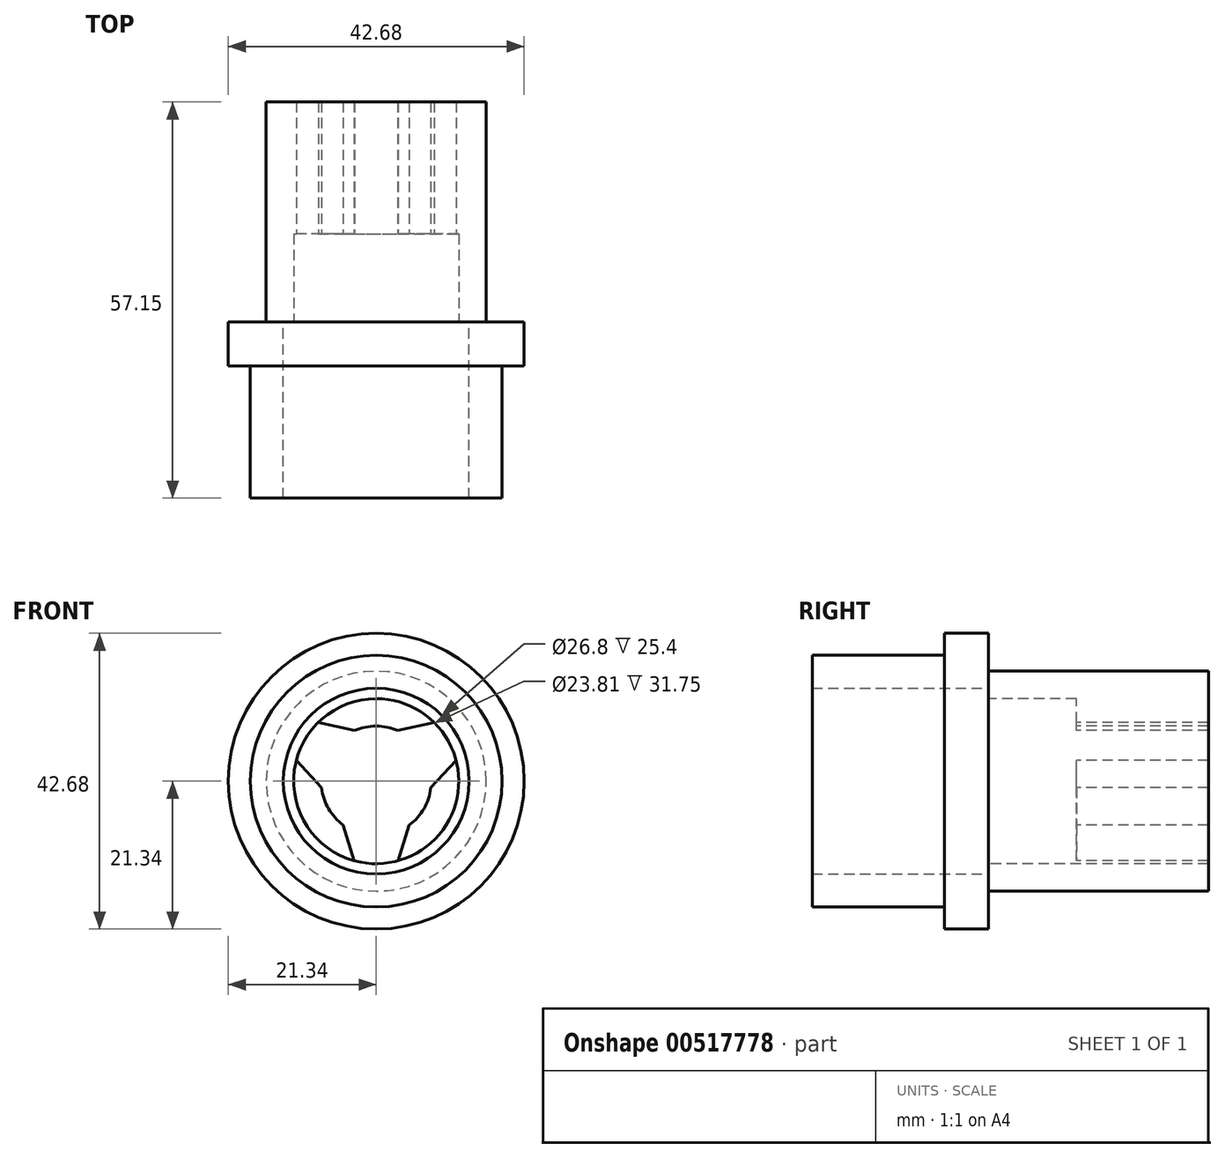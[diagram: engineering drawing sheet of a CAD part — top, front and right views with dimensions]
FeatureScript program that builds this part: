
annotation { "Feature Type Name" : "Feature", "Feature Type Description" : "" }
export const myFeature = defineFeature(function(context is Context, id is Id, definition is map)
    precondition{}
    {
        {
            var Q0;
            Q0=qCreatedBy(makeId("Front.planeOp"),FACE);
            var sketch = newSketch(context, id + "F0", { "sketchPlane" : qUnion([Q0])});
            skCircle(sketch, "E0", {"center": v(0, 0) * mm, "radius": 13.4 * mm});
            skCircle(sketch, "E1", {"center": v(0, 0) * mm, "radius": 18.16 * mm});
            skSolve(sketch);
        }
        {
            var Q0;
            Q0 = qSketchRegion(id + "F0", true);
            extrude(context, id + "F1", {"entities" : qUnion([Q0]), "depth" : 19.05 * mm, "offsetDistance" : 25.4 * mm});
        }
        {
            var Q0;
            Q0=qCreatedBy(makeId("Front.planeOp"),FACE);
            var sketch = newSketch(context, id + "F2", { "sketchPlane" : qUnion([Q0])});
            skCircle(sketch, "E2.0", {"center": v(0, 0) * mm, "radius": 13.4 * mm});
            skCircle(sketch, "E3", {"center": v(0, 0) * mm, "radius": 21.34 * mm});
            skSolve(sketch);
        }
        {
            var Q0;
            Q0 = qSketchRegion(id + "F2", true);
            extrude(context, id + "F3", {"entities" : qUnion([Q0]), "operationType" : NewBodyOperationType.ADD, "oppositeDirection" : true, "depth" : 6.35 * mm, "offsetDistance" : 25.4 * mm});
        }
        {
            var Q0;
            Q0=makeQuery(id+"F3.opExtrude","CAP_FACE",FACE,{"disambiguationData":[OSD([sQuery(id+"F2.wireOp",EDGE,"E2.0"),sQuery(id+"F2.wireOp",EDGE,"E3")])],"isStart":false});
            var sketch = newSketch(context, id + "F4", { "sketchPlane" : qUnion([Q0])});
            skCircle(sketch, "E4", {"center": v(0, 0) * mm, "radius": 11.9 * mm});
            skCircle(sketch, "E5", {"center": v(0, 0) * mm, "radius": 15.88 * mm});
            skSolve(sketch);
        }
        {
            var Q0;
            Q0 = qSketchRegion(id + "F4", true);
            extrude(context, id + "F5", {"entities" : qUnion([Q0]), "operationType" : NewBodyOperationType.ADD, "depth" : 12.7 * mm, "offsetDistance" : 25.4 * mm});
        }
        {
            var Q0;
            Q0=makeQuery(id+"F5.opExtrude","CAP_FACE",FACE,{"disambiguationData":[OSD([sQuery(id+"F4.wireOp",EDGE,"E4"),sQuery(id+"F4.wireOp",EDGE,"E5")])],"isStart":false});
            var sketch = newSketch(context, id + "F6", { "sketchPlane" : qUnion([Q0])});
            skCircle(sketch, "E6.0", {"center": v(0, 0) * mm, "radius": 15.88 * mm});
            skArc(sketch, "E7", {"start": v(-7.88, -0.95) * mm, "mid": v(-6.87, -3.97) * mm, "end": v(-4.76, -6.35) * mm});
            skLineSegment(sketch, "E8", {"start": v(0, 0) * mm, "end": v(0, -15.88) * mm, "construction": true});
            skLineSegment(sketch, "E9", {"start": v(0, 0) * mm, "end": v(-13.75, 7.94) * mm, "construction": true});
            skLineSegment(sketch, "E10", {"start": v(0, 0) * mm, "end": v(13.75, 7.94) * mm, "construction": true});
            skLineSegment(sketch, "E11", {"start": v(-3.12, 7.3) * mm, "end": v(-8.35, 8.49) * mm});
            skLineSegment(sketch, "E12", {"start": v(-7.88, -0.95) * mm, "end": v(-11.53, 2.99) * mm});
            skLineSegment(sketch, "E13", {"start": v(-4.76, -6.35) * mm, "end": v(-3.18, -11.48) * mm});
            skLineSegment(sketch, "E14", {"start": v(4.76, -6.35) * mm, "end": v(3.18, -11.48) * mm});
            skLineSegment(sketch, "E15", {"start": v(7.88, -0.95) * mm, "end": v(11.53, 2.99) * mm});
            skLineSegment(sketch, "E16", {"start": v(3.12, 7.3) * mm, "end": v(8.35, 8.49) * mm});
            skArc(sketch, "E17.0", {"start": v(-8.35, 8.49) * mm, "mid": v(-10.31, 5.95) * mm, "end": v(-11.53, 2.99) * mm});
            skArc(sketch, "E18.trimOffspring", {"start": v(3.12, 7.3) * mm, "mid": v(0, 7.94) * mm, "end": v(-3.12, 7.3) * mm});
            skArc(sketch, "E19.trimOffspring", {"start": v(4.76, -6.35) * mm, "mid": v(6.87, -3.97) * mm, "end": v(7.88, -0.95) * mm});
            skArc(sketch, "E20.trimOffspring", {"start": v(-3.17, -11.48) * mm, "mid": v(0, -11.9) * mm, "end": v(3.18, -11.48) * mm});
            skArc(sketch, "E21.trimOffspring", {"start": v(11.53, 2.99) * mm, "mid": v(10.31, 5.95) * mm, "end": v(8.35, 8.49) * mm});
            skSolve(sketch);
        }
        {
            var Q0;
            Q0 = qSketchRegion(id + "F6", true);
            extrude(context, id + "F7", {"entities" : qUnion([Q0]), "operationType" : NewBodyOperationType.ADD, "depth" : 19.05 * mm, "offsetDistance" : 25.4 * mm});
        }
    });
